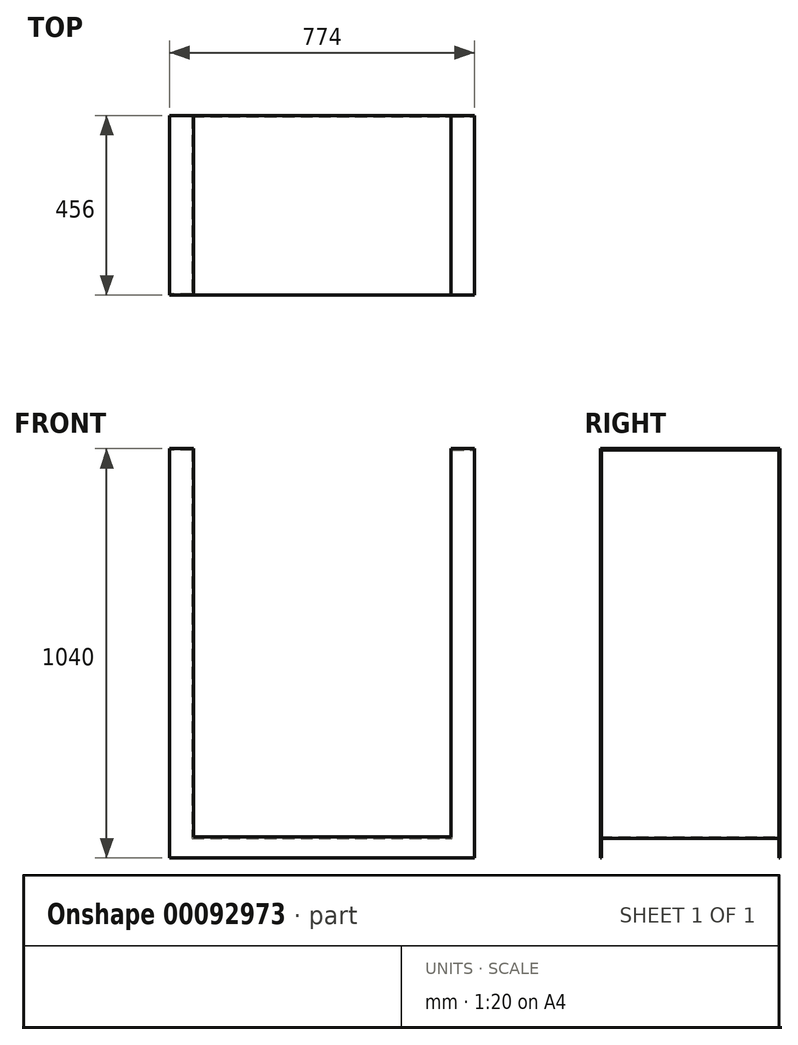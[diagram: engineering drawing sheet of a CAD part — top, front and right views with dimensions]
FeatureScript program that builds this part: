
annotation { "Feature Type Name" : "Feature", "Feature Type Description" : "" }
export const myFeature = defineFeature(function(context is Context, id is Id, definition is map)
    precondition{}
    {
        {
            var Q0;
            Q0=qCreatedBy(makeId("Front.planeOp"),FACE);
            var sketch = newSketch(context, id + "F0", { "sketchPlane" : qUnion([Q0])});
            skLineSegment(sketch, "E0", {"start": v(-330, 990) * mm, "end": v(-330, 0) * mm});
            skLineSegment(sketch, "E1", {"start": v(-330, 0) * mm, "end": v(0, 0) * mm});
            skLineSegment(sketch, "E2", {"start": v(0, 0) * mm, "end": v(330, 0) * mm});
            skLineSegment(sketch, "E3", {"start": v(330, 0) * mm, "end": v(330, 990) * mm});
            skLineSegment(sketch, "E4", {"start": v(330, 990) * mm, "end": v(-330, 990) * mm});
            skLineSegment(sketch, "E5", {"start": v(-200.03, 0) * mm, "end": v(-296.75, 0) * mm, "construction": true});
            skSolve(sketch);
        }
        {
            var Q0;
            Q0=makeQuery(id+"F0.imprint","IMPRINT",FACE,{"disambiguationData":[TD([[makeQuery(id+"F0.imprint","IMPRINT",EDGE,{"derivedFrom":sQuery(id+"F0.wireOp",EDGE,"E0")}),1.0]])]});
            var Q1;
            Q1=sQuery(id+"F0.wireOp",EDGE,"E0");
            var Q2;
            Q2=sQuery(id+"F0.wireOp",EDGE,"E1");
            var Q3;
            Q3=sQuery(id+"F0.wireOp",EDGE,"E2");
            var Q4;
            Q4=sQuery(id+"F0.wireOp",EDGE,"E3");
            extrude(context, id + "F1", {"entities" : qUnion([Q0]), "surfaceEntities" : qUnion([Q1, Q2, Q3, Q4]), "depth" : 450 * mm});
        }
        {
            var Q0;
            Q0=makeQuery(id+"F1.opExtrude","CAP_FACE",FACE,{"disambiguationData":[OSD([sQuery(id+"F0.wireOp",EDGE,"E0"),sQuery(id+"F0.wireOp",EDGE,"E1"),sQuery(id+"F0.wireOp",EDGE,"E2"),sQuery(id+"F0.wireOp",EDGE,"E3"),sQuery(id+"F0.wireOp",EDGE,"E4")])],"isStart":false});
            var Q1;
            Q1=makeQuery(id+"F1.opExtrude","SWEPT_FACE",FACE,{"disambiguationData":[OSD([sQuery(id+"F0.wireOp",EDGE,"E4")])]});
            var Q2;
            Q2=makeQuery(id+"F1.opExtrude","CAP_FACE",FACE,{"disambiguationData":[OSD([sQuery(id+"F0.wireOp",EDGE,"E0"),sQuery(id+"F0.wireOp",EDGE,"E1"),sQuery(id+"F0.wireOp",EDGE,"E2"),sQuery(id+"F0.wireOp",EDGE,"E3"),sQuery(id+"F0.wireOp",EDGE,"E4")])],"isStart":true});
            shell(context, id + "F2", {"entities" : qUnion([Q0, Q1, Q2]), "thickness" : 3 * mm});
        }
        {
            var Q0;
            Q0=makeQuery(id+"F1.opExtrude","SWEPT_FACE",FACE,{"disambiguationData":[OSD([sQuery(id+"F0.wireOp",EDGE,"E4")])]});
            var sketch = newSketch(context, id + "F3", { "sketchPlane" : qUnion([Q0])});
            skLineSegment(sketch, "E6", {"start": v(-387, 0) * mm, "end": v(-387, -450) * mm});
            skLineSegment(sketch, "E7", {"start": v(387, 0) * mm, "end": v(387, -450) * mm});
            skLineSegment(sketch, "E8", {"start": v(-327, 0) * mm, "end": v(-327, -450) * mm});
            skLineSegment(sketch, "E9", {"start": v(-327, -450) * mm, "end": v(-387, -450) * mm});
            skLineSegment(sketch, "E10", {"start": v(-327, 0) * mm, "end": v(-387, 0) * mm});
            skLineSegment(sketch, "E11", {"start": v(327, 0) * mm, "end": v(387, 0) * mm});
            skLineSegment(sketch, "E12", {"start": v(327, 0) * mm, "end": v(327, -450) * mm});
            skLineSegment(sketch, "E13", {"start": v(327, -450) * mm, "end": v(387, -450) * mm});
            skSolve(sketch);
        }
        {
            var Q0;
            Q0 = qSketchRegion(id + "F3", true);
            extrude(context, id + "F4", {"entities" : qUnion([Q0]), "operationType" : NewBodyOperationType.ADD, "oppositeDirection" : true, "depth" : 3 * mm});
        }
        {
            var Q0;
            Q0=makeQuery(id+"F4.boolean.opBoolean","MERGE",FACE,{"derivedFrom":[makeQuery(id+"F1.opExtrude","CAP_FACE",FACE,{"disambiguationData":[OSD([sQuery(id+"F0.wireOp",EDGE,"E0"),sQuery(id+"F0.wireOp",EDGE,"E1"),sQuery(id+"F0.wireOp",EDGE,"E2"),sQuery(id+"F0.wireOp",EDGE,"E3"),sQuery(id+"F0.wireOp",EDGE,"E4")])],"isStart":true}),makeQuery(id+"F4.opExtrude","SWEPT_FACE",FACE,{"disambiguationData":[OSD([sQuery(id+"F3.wireOp",EDGE,"E10")])]}),makeQuery(id+"F4.opExtrude","SWEPT_FACE",FACE,{"disambiguationData":[OSD([sQuery(id+"F3.wireOp",EDGE,"E11")])]})]});
            var sketch = newSketch(context, id + "F5", { "sketchPlane" : qUnion([Q0])});
            skLineSegment(sketch, "E14.0", {"start": v(327, 990) * mm, "end": v(387, 990) * mm});
            skLineSegment(sketch, "E15.0", {"start": v(327, 990) * mm, "end": v(327, 3) * mm});
            skLineSegment(sketch, "E16.0", {"start": v(327, 3) * mm, "end": v(327, 3) * mm});
            skLineSegment(sketch, "E17.0", {"start": v(327, 3) * mm, "end": v(-327, 3) * mm});
            skLineSegment(sketch, "E18.0", {"start": v(-327, 3) * mm, "end": v(-327, 990) * mm});
            skLineSegment(sketch, "E19.0", {"start": v(-387, 990) * mm, "end": v(-327, 990) * mm});
            skLineSegment(sketch, "E20", {"start": v(387, 990) * mm, "end": v(387, -50) * mm});
            skLineSegment(sketch, "E21", {"start": v(-387, 990) * mm, "end": v(-387, -50) * mm});
            skLineSegment(sketch, "E22", {"start": v(-387, -50) * mm, "end": v(22.53, -50) * mm});
            skLineSegment(sketch, "E23", {"start": v(387, -50) * mm, "end": v(22.53, -50) * mm});
            skSolve(sketch);
        }
        {
            var Q0;
            Q0 = qSketchRegion(id + "F5", true);
            extrude(context, id + "F6", {"entities" : qUnion([Q0]), "operationType" : NewBodyOperationType.ADD, "depth" : 3 * mm});
        }
        {
            var Q0;
            Q0=makeQuery(id+"F4.boolean.opBoolean","MERGE",FACE,{"derivedFrom":[makeQuery(id+"F1.opExtrude","CAP_FACE",FACE,{"disambiguationData":[OSD([sQuery(id+"F0.wireOp",EDGE,"E0"),sQuery(id+"F0.wireOp",EDGE,"E1"),sQuery(id+"F0.wireOp",EDGE,"E2"),sQuery(id+"F0.wireOp",EDGE,"E3"),sQuery(id+"F0.wireOp",EDGE,"E4")])],"isStart":false}),makeQuery(id+"F4.opExtrude","SWEPT_FACE",FACE,{"disambiguationData":[OSD([sQuery(id+"F3.wireOp",EDGE,"E9")])]}),makeQuery(id+"F4.opExtrude","SWEPT_FACE",FACE,{"disambiguationData":[OSD([sQuery(id+"F3.wireOp",EDGE,"E13")])]})]});
            var sketch = newSketch(context, id + "F7", { "sketchPlane" : qUnion([Q0])});
            skLineSegment(sketch, "E24.0", {"start": v(387, 990) * mm, "end": v(327, 990) * mm});
            skLineSegment(sketch, "E25.0", {"start": v(327, 3) * mm, "end": v(327, 990) * mm});
            skLineSegment(sketch, "E26.0", {"start": v(-327, 3) * mm, "end": v(327, 3) * mm});
            skLineSegment(sketch, "E27.0", {"start": v(-327, 3) * mm, "end": v(-327, 3) * mm});
            skLineSegment(sketch, "E28.0", {"start": v(-327, 990) * mm, "end": v(-387, 990) * mm});
            skLineSegment(sketch, "E29.0", {"start": v(-327, 990) * mm, "end": v(-327, 3) * mm});
            skLineSegment(sketch, "E30", {"start": v(-387, 990) * mm, "end": v(-387, -50) * mm});
            skLineSegment(sketch, "E31", {"start": v(387, 990) * mm, "end": v(387, -50) * mm});
            skLineSegment(sketch, "E32", {"start": v(-387, -50) * mm, "end": v(35.58, -50) * mm});
            skLineSegment(sketch, "E33", {"start": v(387, -50) * mm, "end": v(35.58, -50) * mm});
            skSolve(sketch);
        }
        {
            var Q0;
            Q0 = qSketchRegion(id + "F7", true);
            extrude(context, id + "F8", {"entities" : qUnion([Q0]), "operationType" : NewBodyOperationType.ADD, "depth" : 3 * mm});
        }
    });
